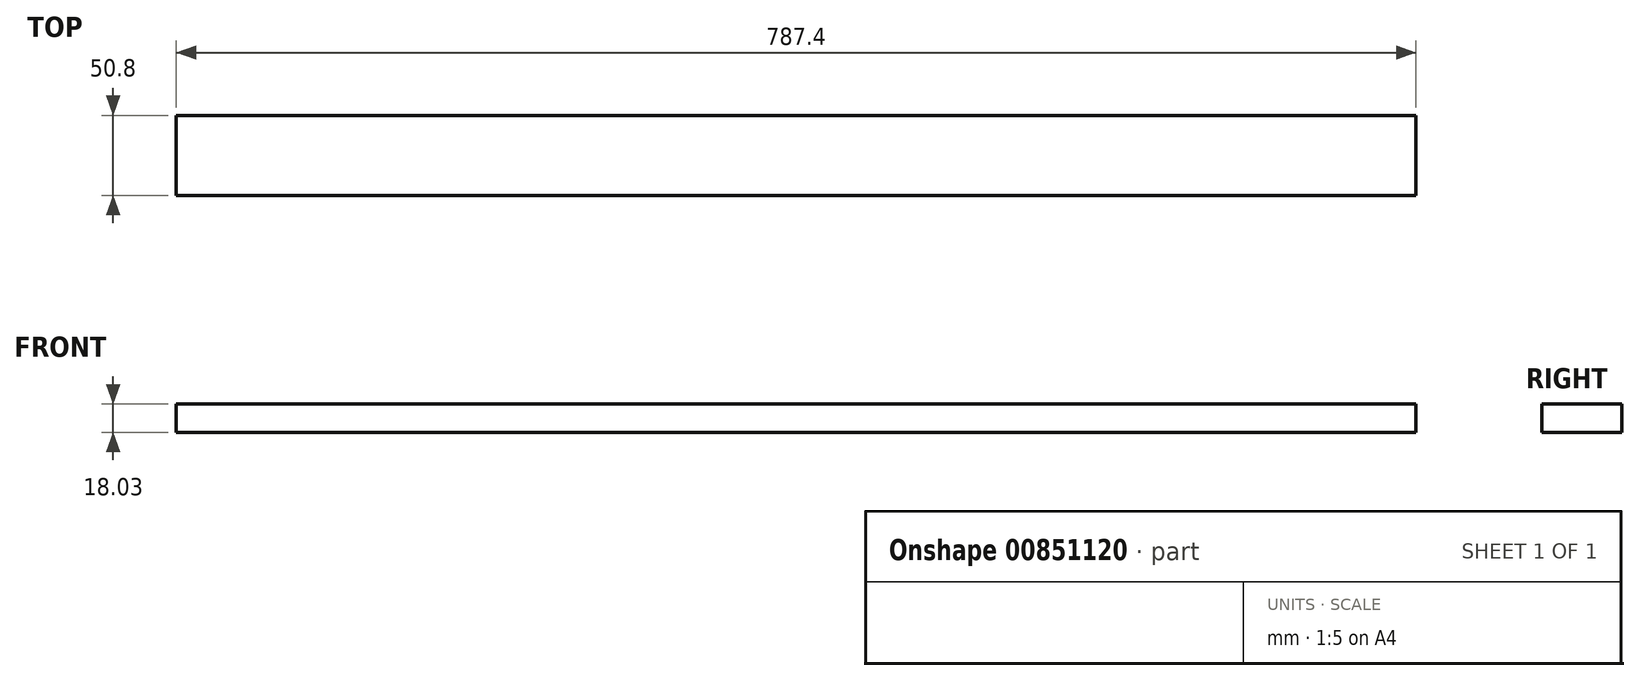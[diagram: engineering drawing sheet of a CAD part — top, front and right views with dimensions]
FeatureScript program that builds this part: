
annotation { "Feature Type Name" : "Feature", "Feature Type Description" : "" }
export const myFeature = defineFeature(function(context is Context, id is Id, definition is map)
    precondition{}
    {
        {
            var Q0;
            Q0=qCreatedBy(makeId("Top.planeOp"),FACE);
            var sketch = newSketch(context, id + "F0", { "sketchPlane" : qUnion([Q0])});
            skLineSegment(sketch, "E0.bottom", {"start": v(-191.13, 29.13) * mm, "end": v(596.27, 29.13) * mm});
            skLineSegment(sketch, "E0.top", {"start": v(-191.13, -21.67) * mm, "end": v(596.27, -21.67) * mm});
            skLineSegment(sketch, "E0.left", {"start": v(-191.13, 29.13) * mm, "end": v(-191.13, -21.67) * mm});
            skLineSegment(sketch, "E0.right", {"start": v(596.27, 29.13) * mm, "end": v(596.27, -21.67) * mm});
            skSolve(sketch);
        }
        {
            var Q0;
            Q0=makeQuery(id+"F0.imprint","IMPRINT",FACE,{"disambiguationData":[TD([[makeQuery(id+"F0.imprint","IMPRINT",EDGE,{"derivedFrom":sQuery(id+"F0.wireOp",EDGE,"E0.bottom")}),-1.0]])]});
            extrude(context, id + "F1", {"entities" : qUnion([Q0]), "depth" : 18.03 * mm, "offsetDistance" : 25.4 * mm});
        }
    });
